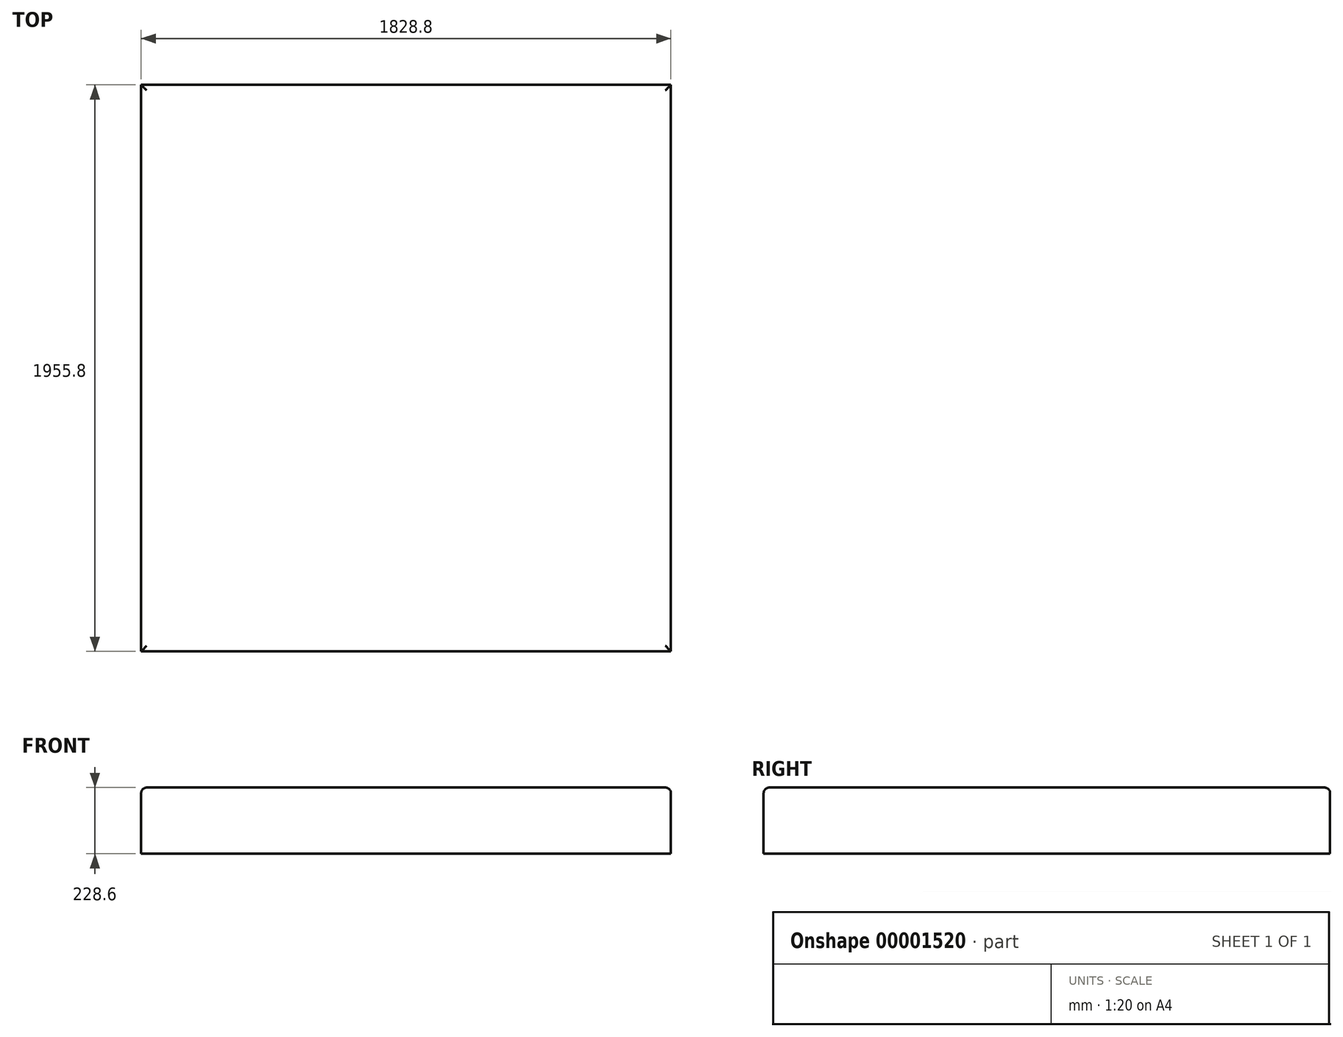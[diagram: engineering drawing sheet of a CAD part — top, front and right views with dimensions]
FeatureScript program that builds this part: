
annotation { "Feature Type Name" : "Feature", "Feature Type Description" : "" }
export const myFeature = defineFeature(function(context is Context, id is Id, definition is map)
    precondition{}
    {
        {
            var Q0;
            Q0=qCreatedBy(makeId("Top.planeOp"),FACE);
            var sketch = newSketch(context, id + "F0", { "sketchPlane" : qUnion([Q0])});
            skLineSegment(sketch, "E0.bottom", {"start": v(0, 0) * mm, "end": v(1828.8, 0) * mm});
            skLineSegment(sketch, "E0.top", {"start": v(0, -1955.8) * mm, "end": v(1828.8, -1955.8) * mm});
            skLineSegment(sketch, "E0.left", {"start": v(0, 0) * mm, "end": v(0, -1955.8) * mm});
            skLineSegment(sketch, "E0.right", {"start": v(1828.8, 0) * mm, "end": v(1828.8, -1955.8) * mm});
            skSolve(sketch);
        }
        {
            var Q0;
            Q0=makeQuery(id+"F0.imprint","IMPRINT",FACE,{"disambiguationData":[TD([[makeQuery(id+"F0.imprint","IMPRINT",EDGE,{"derivedFrom":sQuery(id+"F0.wireOp",EDGE,"E0.bottom")}),-1.0]])]});
            extrude(context, id + "F1", {"entities" : qUnion([Q0]), "depth" : 228.6 * mm});
        }
        {
            var Q0;
            Q0=makeQuery(id+"F1.opExtrude","CAP_EDGE",EDGE,{"disambiguationData":[OSD([sQuery(id+"F0.wireOp",EDGE,"E0.top")])],"isStart":false});
            var Q1;
            Q1=makeQuery(id+"F1.opExtrude","CAP_EDGE",EDGE,{"disambiguationData":[OSD([sQuery(id+"F0.wireOp",EDGE,"E0.left")])],"isStart":false});
            var Q2;
            Q2=makeQuery(id+"F1.opExtrude","CAP_EDGE",EDGE,{"disambiguationData":[OSD([sQuery(id+"F0.wireOp",EDGE,"E0.bottom")])],"isStart":false});
            var Q3;
            Q3=makeQuery(id+"F1.opExtrude","CAP_EDGE",EDGE,{"disambiguationData":[OSD([sQuery(id+"F0.wireOp",EDGE,"E0.right")])],"isStart":false});
            fillet(context, id + "F2", {"entities" : qUnion([Q0, Q1, Q2, Q3]), "radius" : 19.05 * mm, "tangentPropagation" : true, "allowEdgeOverflow" : false});
        }
    });
